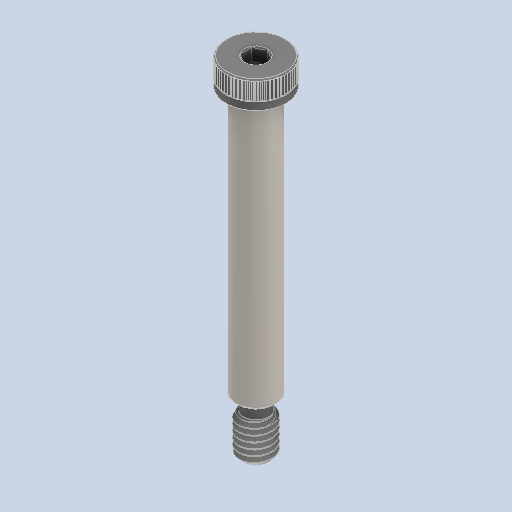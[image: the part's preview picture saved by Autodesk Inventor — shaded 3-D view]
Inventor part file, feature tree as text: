
AUTODESK INVENTOR PART (.ipt)
format: ipt  version: 2023.2 (Build 272271000, 271)  size: 428,032 bytes
history: native  units: in
note: dims shown in document units (in); Inventor stores cm internally (conversion verified against a paired STEP export)
features: chamfer x1
ambient origin geometry x8: Origin, YZ Plane, XZ Plane, XY Plane, X Axis, Y Axis, Z Axis, Center Point
bodies: Solid1 (feature_tree)
feature tree (1):
  chamfer  "Chamfer3"  [1 undecoded]
note: 1 required parameter value undecoded (feature->parameter linkage not recoverable at this tier; creation-order binding heuristic only, values carry confidence <= 0.55)
